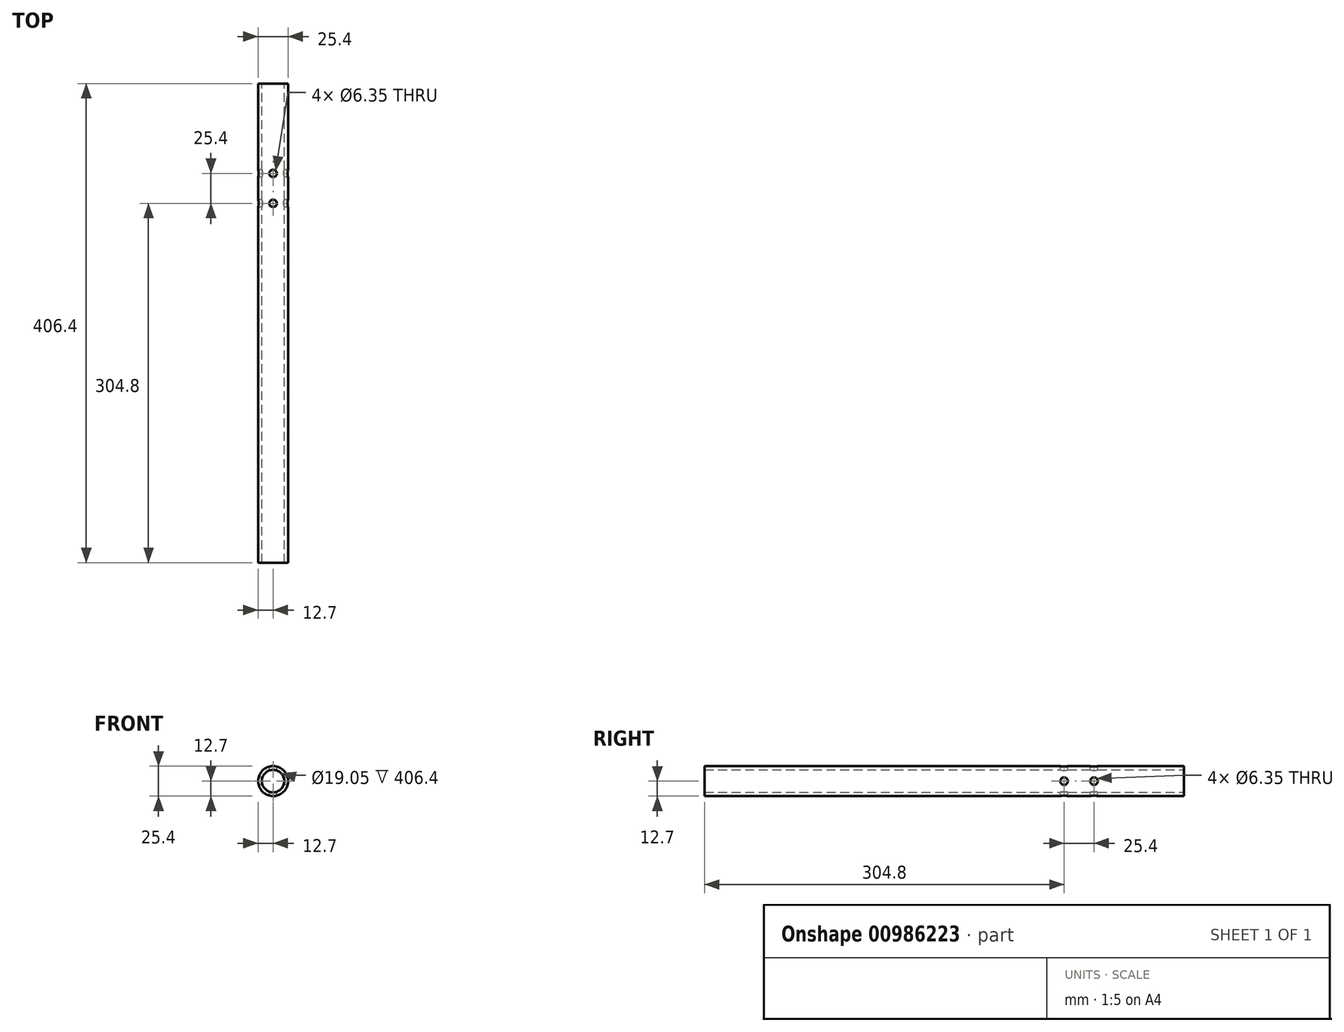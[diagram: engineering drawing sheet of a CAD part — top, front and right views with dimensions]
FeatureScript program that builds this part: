
annotation { "Feature Type Name" : "Feature", "Feature Type Description" : "" }
export const myFeature = defineFeature(function(context is Context, id is Id, definition is map)
    precondition{}
    {
        {
            var Q0;
            Q0=qCreatedBy(makeId("Front.planeOp"),FACE);
            var sketch = newSketch(context, id + "F0", { "sketchPlane" : qUnion([Q0])});
            skCircle(sketch, "E0", {"center": v(0, 0) * mm, "radius": 12.7 * mm});
            skCircle(sketch, "E1.0", {"center": v(0, 0) * mm, "radius": 9.53 * mm});
            skSolve(sketch);
        }
        {
            var Q0;
            Q0=makeQuery(id+"F0.imprint","IMPRINT",FACE,{"disambiguationData":[TD([[makeQuery(id+"F0.imprint","IMPRINT",EDGE,{"derivedFrom":sQuery(id+"F0.wireOp",EDGE,"E0")}),1.0]])]});
            extrude(context, id + "F1", {"entities" : qUnion([Q0]), "depth" : 406.4 * mm, "offsetDistance" : 25.4 * mm});
        }
        {
            var Q0;
            Q0=qCreatedBy(makeId("Right.planeOp"),FACE);
            var sketch = newSketch(context, id + "F2", { "sketchPlane" : qUnion([Q0])});
            skCircle(sketch, "E2", {"center": v(-76.2, 0) * mm, "radius": 3.18 * mm});
            skCircle(sketch, "E3", {"center": v(-101.6, 0) * mm, "radius": 3.18 * mm});
            skSolve(sketch);
        }
        {
            var Q0;
            Q0=makeQuery(id+"F2.imprint","IMPRINT",FACE,{"disambiguationData":[TD([[makeQuery(id+"F2.imprint","IMPRINT",EDGE,{"derivedFrom":sQuery(id+"F2.wireOp",EDGE,"E3")}),1.0]])]});
            var Q1;
            Q1=makeQuery(id+"F2.imprint","IMPRINT",FACE,{"disambiguationData":[TD([[makeQuery(id+"F2.imprint","IMPRINT",EDGE,{"derivedFrom":sQuery(id+"F2.wireOp",EDGE,"E2")}),1.0]])]});
            var Q2;
            Q2=sQuery(id+"F2.wireOp",EDGE,"E3");
            var Q3;
            Q3=sQuery(id+"F2.wireOp",EDGE,"E2");
            extrude(context, id + "F3", {"entities" : qUnion([Q0, Q1]), "operationType" : NewBodyOperationType.REMOVE, "surfaceEntities" : qUnion([Q2, Q3]), "endBound" : BoundingType.SYMMETRIC, "depth" : 25.4 * mm, "offsetDistance" : 25.4 * mm});
        }
        {
            var Q0;
            Q0=qCreatedBy(makeId("Top.planeOp"),FACE);
            var sketch = newSketch(context, id + "F4", { "sketchPlane" : qUnion([Q0])});
            skCircle(sketch, "E4", {"center": v(0, -76.2) * mm, "radius": 3.18 * mm});
            skCircle(sketch, "E5", {"center": v(0, -101.6) * mm, "radius": 3.18 * mm});
            skSolve(sketch);
        }
        {
            var Q0;
            Q0=makeQuery(id+"F4.imprint","IMPRINT",FACE,{"disambiguationData":[TD([[makeQuery(id+"F4.imprint","IMPRINT",EDGE,{"derivedFrom":sQuery(id+"F4.wireOp",EDGE,"E4")}),1.0]])]});
            var Q1;
            Q1=makeQuery(id+"F4.imprint","IMPRINT",FACE,{"disambiguationData":[TD([[makeQuery(id+"F4.imprint","IMPRINT",EDGE,{"derivedFrom":sQuery(id+"F4.wireOp",EDGE,"E5")}),1.0]])]});
            extrude(context, id + "F5", {"entities" : qUnion([Q0, Q1]), "operationType" : NewBodyOperationType.REMOVE, "endBound" : BoundingType.SYMMETRIC, "oppositeDirection" : true, "depth" : 25.4 * mm, "offsetDistance" : 25.4 * mm});
        }
    });
